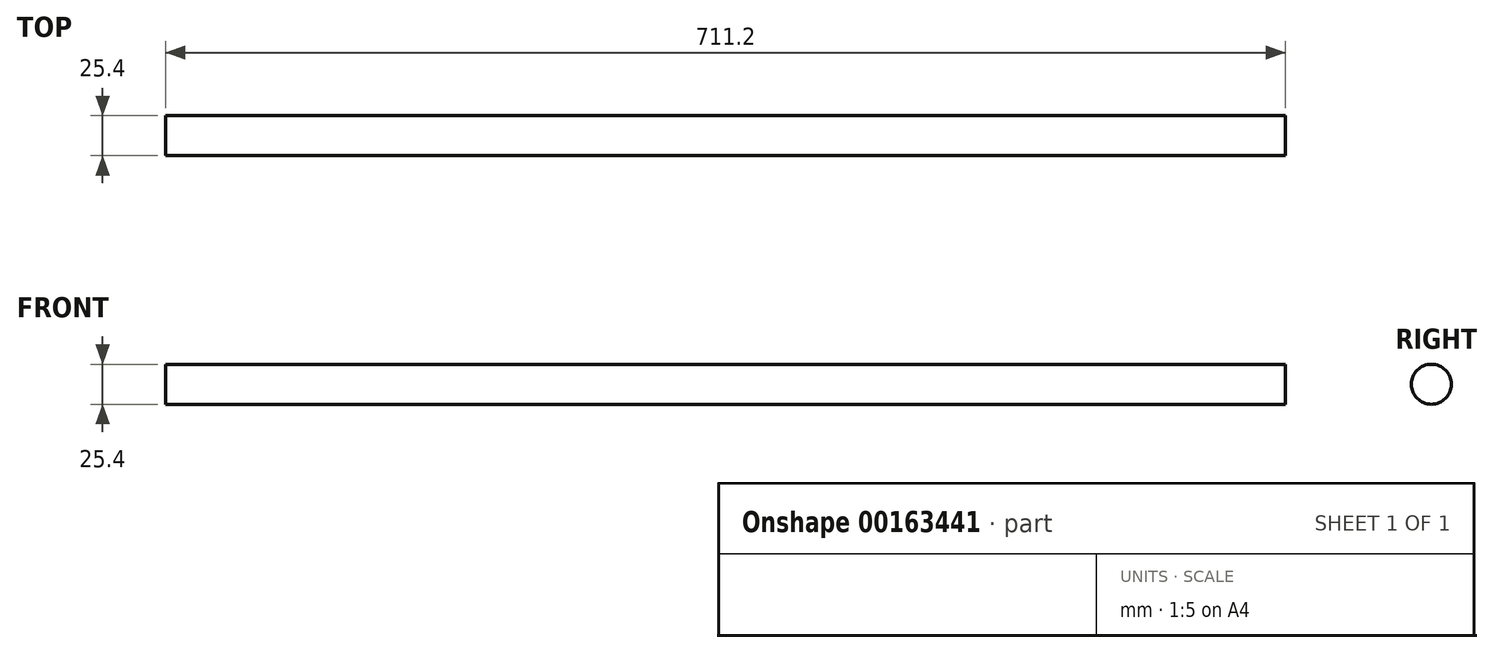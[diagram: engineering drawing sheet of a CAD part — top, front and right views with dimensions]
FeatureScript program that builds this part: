
annotation { "Feature Type Name" : "Feature", "Feature Type Description" : "" }
export const myFeature = defineFeature(function(context is Context, id is Id, definition is map)
    precondition{}
    {
        {
            var Q0;
            Q0=qCreatedBy(makeId("Right.planeOp"),FACE);
            var sketch = newSketch(context, id + "F0", { "sketchPlane" : qUnion([Q0])});
            skCircle(sketch, "E0", {"center": v(0, 0) * mm, "radius": 12.7 * mm});
            skSolve(sketch);
        }
        {
            var Q0;
            Q0 = qSketchRegion(id + "F0", true);
            extrude(context, id + "F1", {"entities" : qUnion([Q0]), "depth" : 711.2 * mm});
        }
    });
